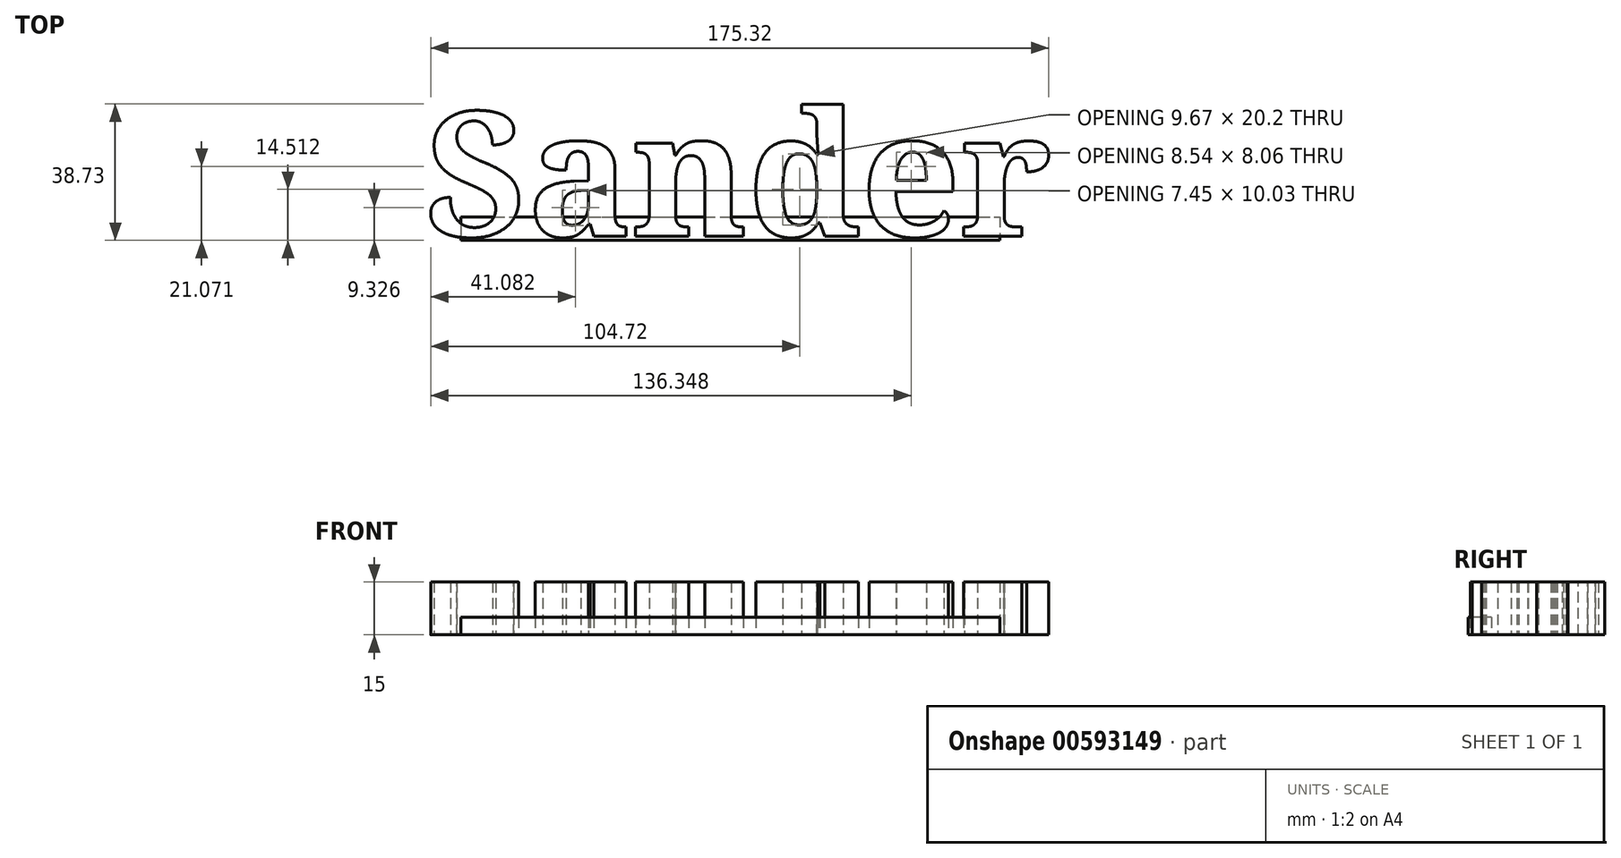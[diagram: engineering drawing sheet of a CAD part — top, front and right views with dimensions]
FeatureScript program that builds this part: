
annotation { "Feature Type Name" : "Feature", "Feature Type Description" : "" }
export const myFeature = defineFeature(function(context is Context, id is Id, definition is map)
    precondition{}
    {
        {
            var Q0;
            Q0=qCreatedBy(makeId("Top.planeOp"),FACE);
            var sketch = newSketch(context, id + "F0", { "sketchPlane" : qUnion([Q0])});
            skText(sketch, "E0", { "text": "Sander", "fontName": "NotoSerif-Bold.ttf"});
            const initialGuessF0  = {"E0": [-0.09, -0.0183, 1, 0, 0.03556]};
            skSetInitialGuess(sketch, initialGuessF0);
            skSolve(sketch);
        }
        {
            var Q0;
            Q0=qCreatedBy(makeId("Top.planeOp"),FACE);
            var sketch = newSketch(context, id + "F1", { "sketchPlane" : qUnion([Q0])});
            skLineSegment(sketch, "E1.bottom", {"start": v(-80, -12.8) * mm, "end": v(73, -12.8) * mm});
            skLineSegment(sketch, "E1.top", {"start": v(-80, -19.5) * mm, "end": v(73, -19.5) * mm});
            skLineSegment(sketch, "E1.left", {"start": v(-80, -12.8) * mm, "end": v(-80, -19.5) * mm});
            skLineSegment(sketch, "E1.right", {"start": v(73, -12.8) * mm, "end": v(73, -19.5) * mm});
            skSolve(sketch);
        }
        {
            var Q0;
            Q0 = qSketchRegion(id + "F0", true);
            extrude(context, id + "F2", {"entities" : qUnion([Q0]), "depth" : 15 * mm, "offsetDistance" : 25 * mm});
        }
        {
            var Q0;
            Q0 = qSketchRegion(id + "F1", true);
            extrude(context, id + "F3", {"entities" : qUnion([Q0]), "depth" : 5 * mm, "offsetDistance" : 25 * mm});
        }
    });
